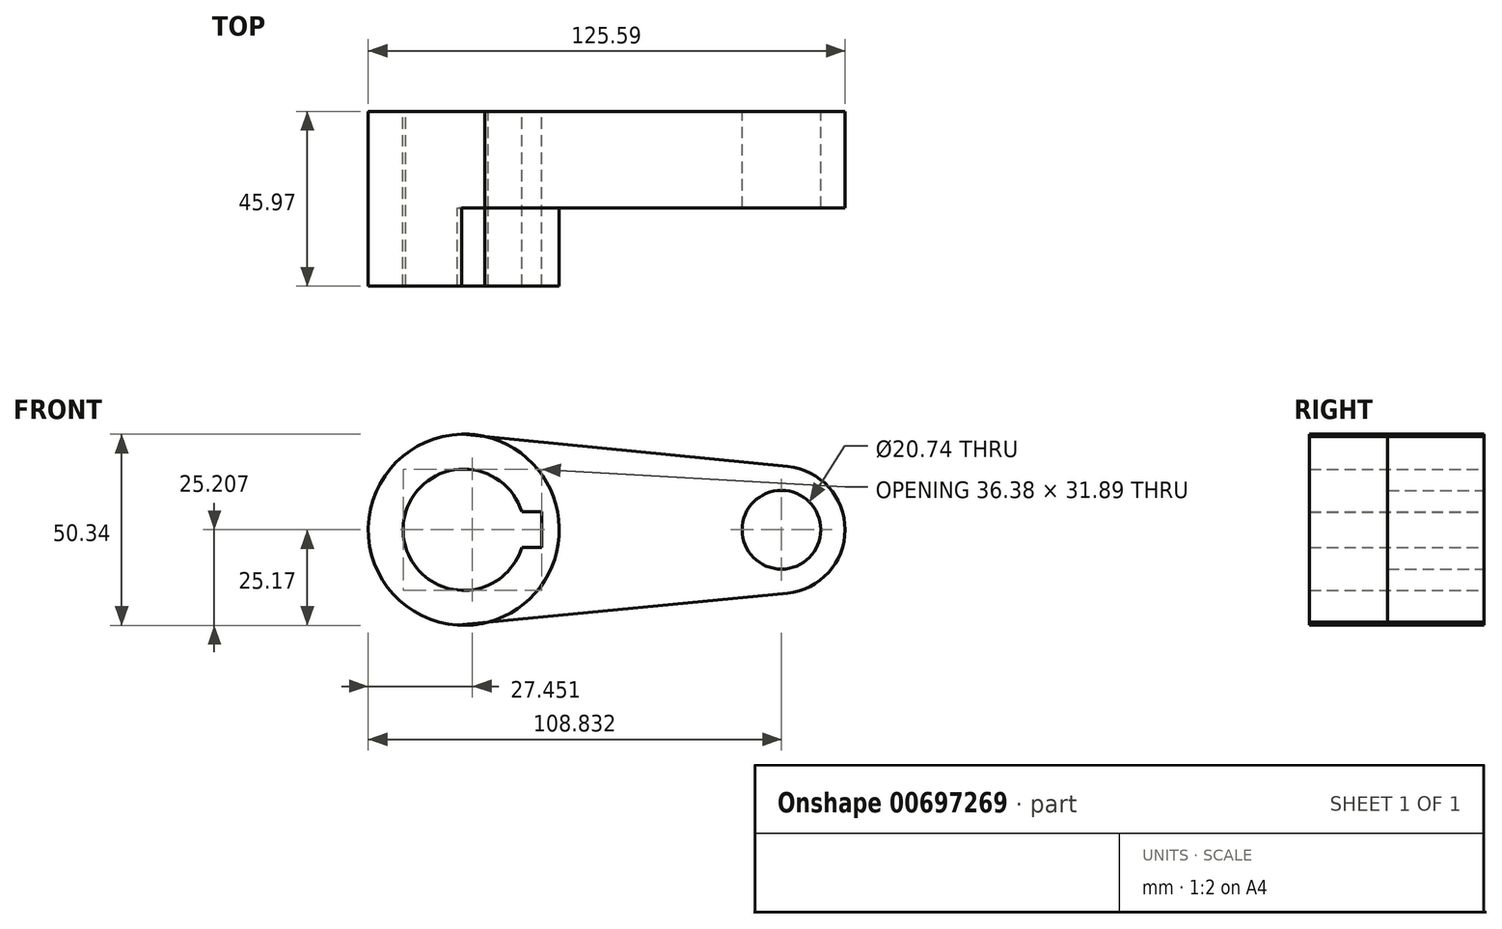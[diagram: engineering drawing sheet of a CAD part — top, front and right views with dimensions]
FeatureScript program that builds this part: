
annotation { "Feature Type Name" : "Feature", "Feature Type Description" : "" }
export const myFeature = defineFeature(function(context is Context, id is Id, definition is map)
    precondition{}
    {
        {
            var Q0;
            Q0=qCreatedBy(makeId("Front.planeOp"),FACE);
            var sketch = newSketch(context, id + "F0", { "sketchPlane" : qUnion([Q0])});
            skCircle(sketch, "E0", {"center": v(-41.4, 0) * mm, "radius": 25.17 * mm});
            skCircle(sketch, "E1", {"center": v(42.27, 0) * mm, "radius": 16.75 * mm});
            skCircle(sketch, "E2", {"center": v(-41.4, 0) * mm, "radius": 15.98 * mm});
            skCircle(sketch, "E3", {"center": v(42.27, 0) * mm, "radius": 10.37 * mm});
            skLineSegment(sketch, "E4", {"start": v(-41.98, 25.16) * mm, "end": v(43.92, 16.67) * mm});
            skLineSegment(sketch, "E5", {"start": v(-43.07, -25.1) * mm, "end": v(43.89, -16.68) * mm});
            skLineSegment(sketch, "E6.bottom", {"start": v(-20.92, 4.68) * mm, "end": v(-56.68, 4.68) * mm});
            skLineSegment(sketch, "E6.top", {"start": v(-20.92, -4.67) * mm, "end": v(-56.68, -4.67) * mm});
            skLineSegment(sketch, "E6.left", {"start": v(-20.92, 4.68) * mm, "end": v(-20.92, -4.67) * mm});
            skLineSegment(sketch, "E6.right", {"start": v(-56.68, 4.68) * mm, "end": v(-56.68, -4.67) * mm});
            skSolve(sketch);
        }
        {
            var Q0;
            Q0 = qSketchRegion(id + "F0", true);
            extrude(context, id + "F1", {"entities" : qUnion([Q0]), "depth" : 25.4 * mm, "offsetDistance" : 25.4 * mm});
        }
        {
            var Q0;
            {var subQ5=sQuery(id+"F0.wireOp",EDGE,"E6.left");Q0=makeQuery(id+"F0.imprint","IMPRINT",FACE,{"disambiguationData":[TD([[makeQuery(id+"F0.imprint","IMPRINT",EDGE,{"derivedFrom":subQ5}),1.0]])]});}
            extrude(context, id + "F2", {"entities" : qUnion([Q0]), "operationType" : NewBodyOperationType.ADD, "depth" : 45.97 * mm, "offsetDistance" : 25.4 * mm});
        }
    });
